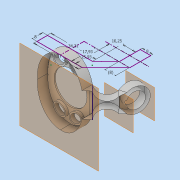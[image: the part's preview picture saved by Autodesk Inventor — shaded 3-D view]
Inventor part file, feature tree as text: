
AUTODESK INVENTOR PART (.ipt)
format: ipt  version: 2019 (Build 230136000, 136)  size: 535,552 bytes
history: native  units: mm
features: other x22, sketch x8, extrude x5, loft x3, projected_geometry x2, shell x1
ambient origin geometry x8: Origin, YZ Plane, XZ Plane, XY Plane, X Axis, Y Axis, Z Axis, Center Point
bodies: Body1 (feature_tree), Body2 (feature_tree), Body3 (feature_tree), Body4 (feature_tree)
feature tree (41):
  other  "Твердое тело1"
  other  "Основной эскиз"
  extrude  "ВыдавливаниеОсновной"  Depth=34.31mm
  other  "РабПлоскость18"
  other  "РабПлоскость41"
  other  "Ручка"
  other  "РабПлоскость49"
  other  "РабПлоскость50"
  loft  "Лофт15"
  extrude  "Выдавливание32"  Depth=34.31mm
  sketch  "Эскиз37"
  other  "РабПлоскость45"
  extrude  "Выдавливание35"  Depth=8.0mm
  extrude  "Корпус элипса"  Depth=17.93mm
  extrude  "Дырки"  Depth=25.93mm
  loft  "Лофт25"
  sketch  "Эскиз43"
  sketch  "Эскиз44"
  other  "РабПлоскость46"
  loft  "Лофт27"
  shell  "Оболочка15"  Thickness=49.49mm
  other  "Удаление грани34"
  other  "Удаление грани35"
  other  "Удаление грани36"
  other  "Удаление грани37"
  other  "Удаление грани38"
  other  "Удаление грани39"
  other  "Отвертстия"
  other  "Твердое тело13"
  sketch  "Эскиз33"
  sketch  "Эскиз34"
  other  "Твердое тело18"
  sketch  "Эскиз38"
  other  "Твердое тело24"
  sketch  "Эскиз42"
  other  "Ребра55"
  other  "Ребра56"
  projected_geometry  "Спроецированная петля7"
  sketch  "Эскиз46"
  projected_geometry  "Спроецированная петля8"
  other  "Ребра57"
